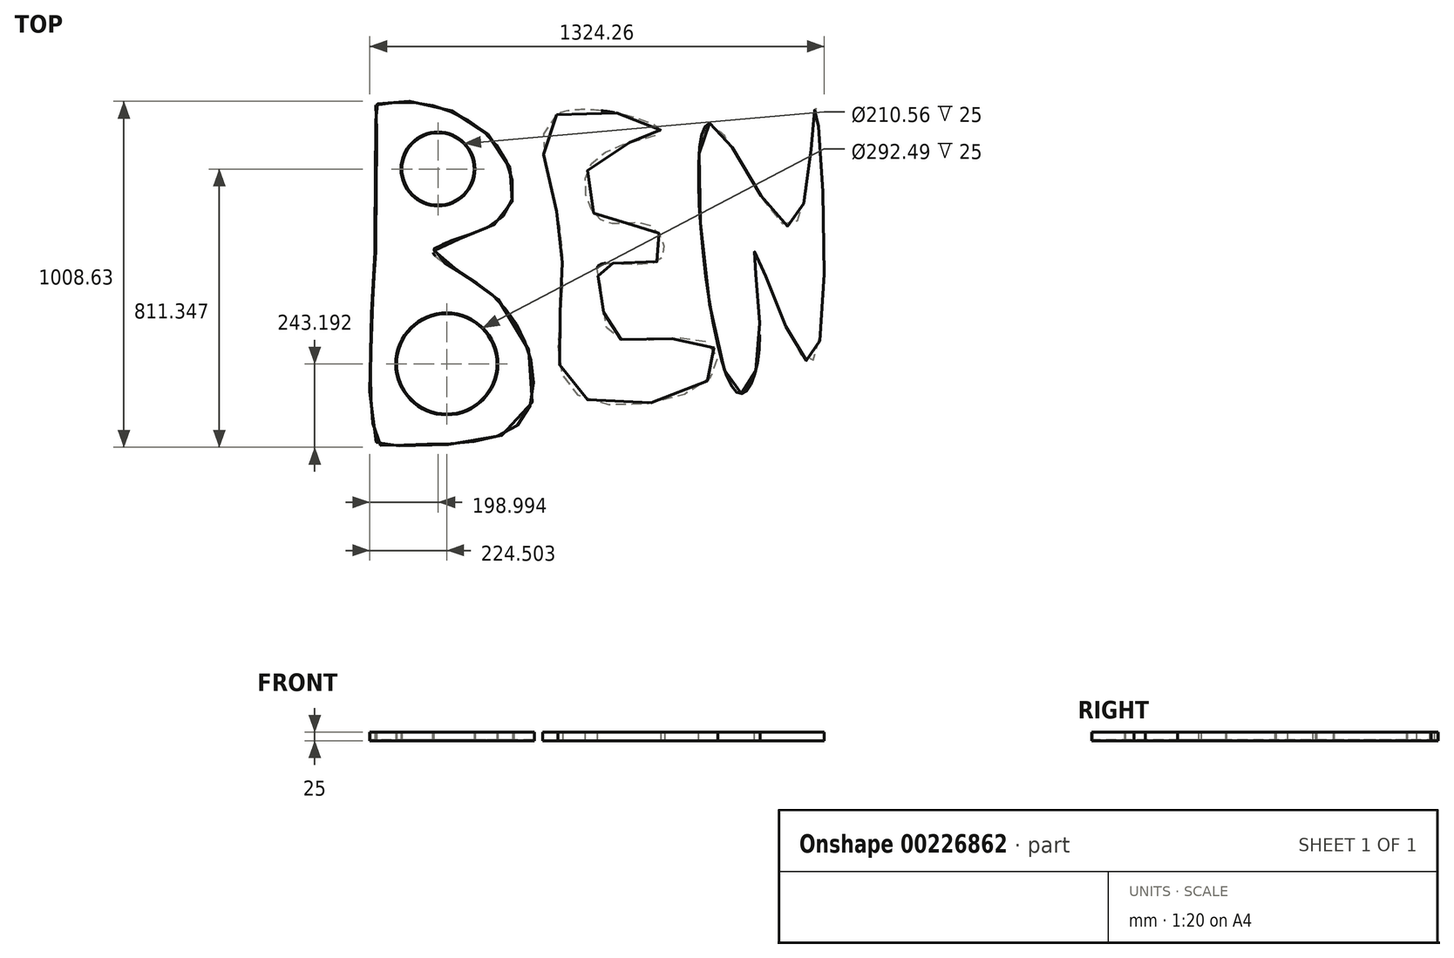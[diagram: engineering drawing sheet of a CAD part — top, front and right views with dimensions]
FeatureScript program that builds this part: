
annotation { "Feature Type Name" : "Feature", "Feature Type Description" : "" }
export const myFeature = defineFeature(function(context is Context, id is Id, definition is map)
    precondition{}
    {
        {
            var Q0;
            Q0=qCreatedBy(makeId("Top.planeOp"),FACE);
            var sketch = newSketch(context, id + "F0", { "sketchPlane" : qUnion([Q0])});
            skFitSpline(sketch, "E0", {"points": [v(0, 0) * mm, v(0, 368.93) * mm, v(0, 372.74) * mm, v(122.08, 380.37) * mm, v(350.82, 262.19) * mm, v(400.38, 90.64) * mm, v(301.26, 0) * mm, v(171.64, -54.23) * mm, v(369.88, -206.72) * mm, v(423.25, -557.45) * mm, v(72.52, -622.26) * mm, v(0, -603.2) * mm, v(0, -38.98) * mm, v(0, 0) * mm]});
            skCircle(sketch, "E1", {"center": v(183.67, 184.99) * mm, "radius": 105.28 * mm});
            skCircle(sketch, "E2", {"center": v(209.18, -383.17) * mm, "radius": 146.24 * mm});
            skSolve(sketch);
        }
        {
            var Q0;
            Q0=qCreatedBy(makeId("Top.planeOp"),FACE);
            var sketch = newSketch(context, id + "F1", { "sketchPlane" : qUnion([Q0])});
            skFitSpline(sketch, "E3", {"points": [v(529.36, 343.7) * mm, v(525.5, 77.53) * mm, v(540.93, -221.43) * mm, v(591.08, -474.1) * mm, v(976.84, -423.95) * mm, v(963.34, -317.87) * mm, v(697.17, -304.37) * mm, v(660.52, -165.5) * mm, v(654.73, -94.13) * mm, v(832.18, -78.7) * mm, v(803.25, 19.67) * mm, v(660.52, 35.1) * mm, v(639.3, 210.62) * mm, v(832.18, 297.41) * mm, v(529.36, 343.7) * mm]});
            skSolve(sketch);
        }
        {
            var Q0;
            Q0=qCreatedBy(makeId("Top.planeOp"),FACE);
            var sketch = newSketch(context, id + "F2", { "sketchPlane" : qUnion([Q0])});
            skFitSpline(sketch, "E4", {"points": [v(974.91, 318.63) * mm, v(1046.28, -458.67) * mm, v(1119.57, -342.95) * mm, v(1109.93, -59.41) * mm, v(1271.94, -375.73) * mm, v(1283.52, 362.99) * mm, v(1214.08, 17.74) * mm, v(974.91, 318.63) * mm]});
            skSolve(sketch);
        }
        {
            var Q0;
            Q0=makeQuery(id+"F1.imprint","IMPRINT",FACE,{"disambiguationData":[TD([[makeQuery(id+"F1.imprint","IMPRINT",EDGE,{"derivedFrom":sQuery(id+"F1.wireOp",EDGE,"E3")}),1.0]])]});
            var Q1;
            Q1=makeQuery(id+"F2.imprint","IMPRINT",FACE,{"disambiguationData":[TD([[makeQuery(id+"F2.imprint","IMPRINT",EDGE,{"derivedFrom":sQuery(id+"F2.wireOp",EDGE,"E4")}),1.0]])]});
            var Q2;
            Q2=makeQuery(id+"F0.imprint","IMPRINT",FACE,{"disambiguationData":[TD([[makeQuery(id+"F0.imprint","IMPRINT",EDGE,{"derivedFrom":sQuery(id+"F0.wireOp",EDGE,"E0")}),-1.0]])]});
            extrude(context, id + "F3", {"entities" : qUnion([Q0, Q1, Q2]), "depth" : 25 * mm});
        }
        {
            var Q0;
            Q0=makeQuery(id+"F3.opExtrude","CAP_FACE",FACE,{"disambiguationData":[OSD([sQuery(id+"F0.wireOp",EDGE,"E0")])],"isStart":false});
            shell(context, id + "F4", {"entities" : qUnion([Q0]), "thickness" : 2.5 * mm});
        }
    });
